# Revit family: 706600001_Barra de Seguiridad Sanitaria Tipo H
name_source: partatom
category: Plumbing Fixtures
units: mm (PartAtom-declared; Revit-internal decimal feet)

## family parameters
Always vertical = Yes
Cut with Voids When Loaded = No
Host = Wall
OmniClass Number = 23.31.00.00
OmniClass Title = Plumbing Specific Products and Equipment
Part Type = Normal
Room Calculation Point = No
Round Connector Dimension = Use Diameter
Shared = No

## types (1)
- Type 1
    Alto = 406 mm
    Ancho = 750 mm
    Capacidad de Funcionamiento = Soporta una carga hasta de 150 Kg.
    Creado por = BIMBAU
    Cuidado Y Limpieza = Para prolongar y preservar las cualidades del acero es vital que la limpieza profunda del producto se haga únicamente con agua y jabón suave y que en el secado y el brillo se utilice un paño de
algodón limpio, dicha limpieza se recomienda 2 veces a la semana, y en zonas costeras a diario por la salinidad del ambiente. Por ningún motivo deben usarse elementos abrasivos, ácidos o disolventes para la limpieza del producto. (ácido muriático, ácido sulfúrico, yodo, derivados del cloro, amoniaco, blanqueadores.)
Los acabados pueden variar su comportamiento en zonas costeras y/o en ambientes corrosivos. En referencias satinadas limpie en el
sentido del pulido del acero.
    Default Elevation = 0 mm  [stored 0 ft]
    Description = Barra de seguridad ideal para personas con movilidad reducida, cumple cumple requerimientos ADA. Elemento de mobiliario para el apoyo, seguridad y protección de usuarios. Con características y dimensiones ergonómicamente adecuadas para su uso. Por su diseño ayuda al usuario a soportar el peso del cuerpo y
así utilizar de la mejor manera el inodoro.
    Escudo Metálico = Material metálico, mayor durabilidad y excelentes propiedades mecánicas.
    Fecha de creación = 09/04/2021
    Garantía = 1 Año
    Material = Corona_Acero inoxidable
    Profundidad = 579 mm
    Referencia = 706600001
    Resistencia = Corrosión, pelado y decoloración por agua
    Sistema de Instalación = Fácil instalación por medio de chazos y tornillos anclados a la pared que ofrecen gran seguridad.
    URL = https://corona.co
    Uso = Doméstico e institucional.

note: [stored X ft] marks values corroborated as IEEE doubles in the binary element streams (Revit-internal decimal feet)

## geometry (parser evidence)
native form markers: Sweep x3
no freeform markers — native parametric forms only
